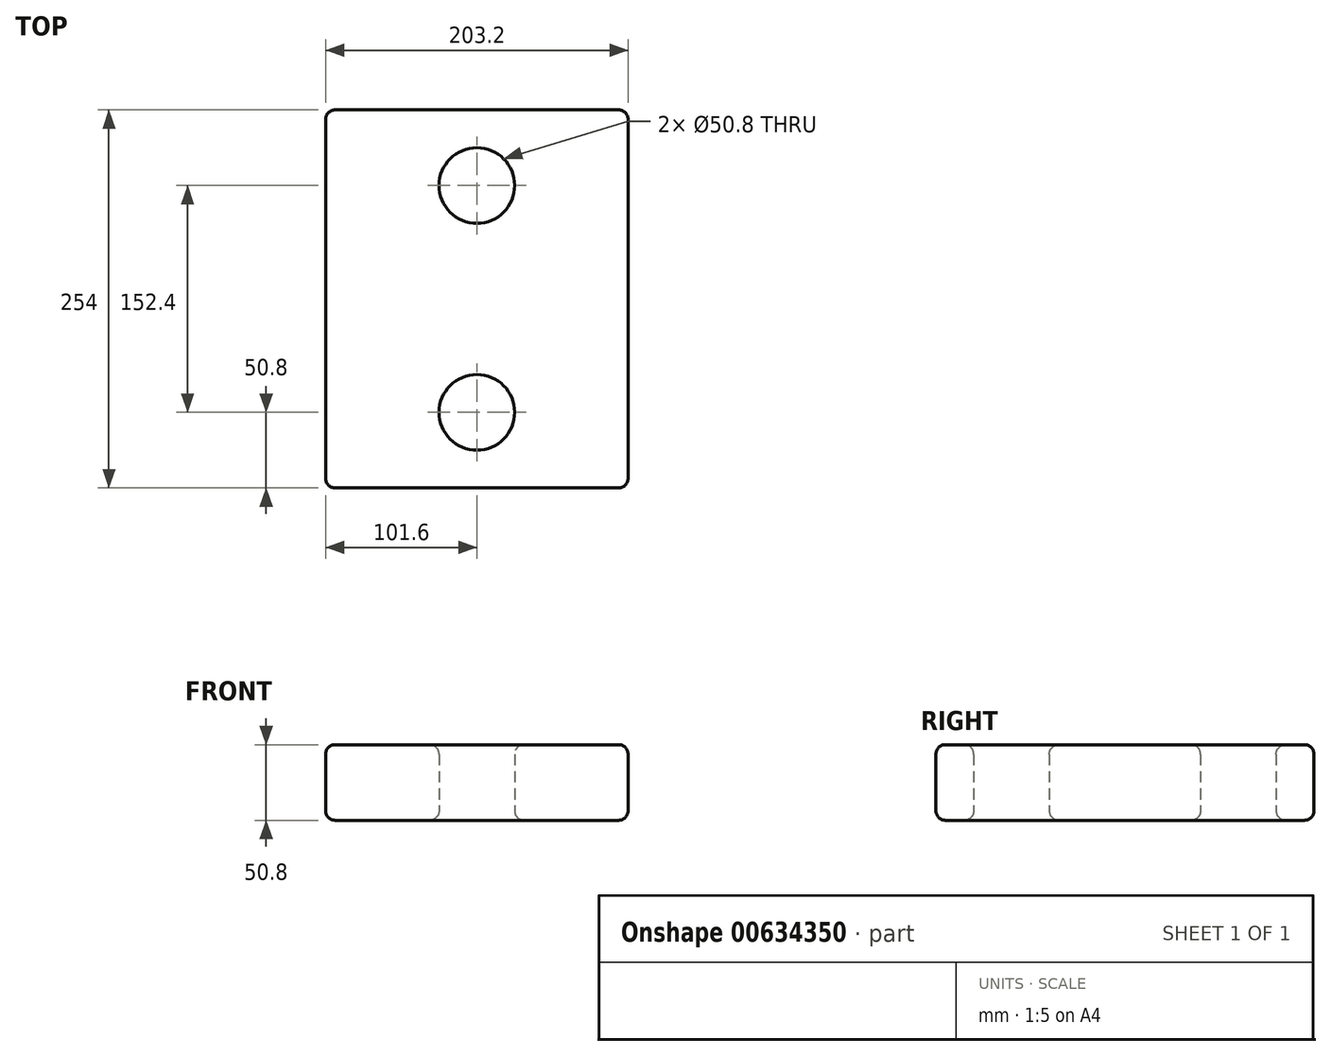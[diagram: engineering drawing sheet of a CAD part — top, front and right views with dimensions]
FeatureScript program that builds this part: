
annotation { "Feature Type Name" : "Feature", "Feature Type Description" : "" }
export const myFeature = defineFeature(function(context is Context, id is Id, definition is map)
    precondition{}
    {
        {
            var Q0;
            Q0=qCreatedBy(makeId("Top.planeOp"),FACE);
            var sketch = newSketch(context, id + "F0", { "sketchPlane" : qUnion([Q0])});
            skLineSegment(sketch, "E0.bottom", {"start": v(0, 0) * mm, "end": v(203.2, 0) * mm});
            skLineSegment(sketch, "E0.top", {"start": v(0, 254) * mm, "end": v(203.2, 254) * mm});
            skLineSegment(sketch, "E0.left", {"start": v(0, 0) * mm, "end": v(0, 254) * mm});
            skLineSegment(sketch, "E0.right", {"start": v(203.2, 0) * mm, "end": v(203.2, 254) * mm});
            skCircle(sketch, "E1", {"center": v(101.6, 203.2) * mm, "radius": 25.4 * mm});
            skPoint(sketch, "E1.centerSnap0", {"position": v(101.6, 0) * mm});
            skLineSegment(sketch, "E2", {"start": v(0, 127) * mm, "end": v(203.2, 127) * mm, "construction": true});
            skCircle(sketch, "E3.MirrorC", {"center": v(101.6, 50.8) * mm, "radius": 25.4 * mm});
            skSolve(sketch);
        }
        {
            var Q0;
            Q0=makeQuery(id+"F0.imprint","IMPRINT",FACE,{"disambiguationData":[TD([[makeQuery(id+"F0.imprint","IMPRINT",EDGE,{"derivedFrom":sQuery(id+"F0.wireOp",EDGE,"E0.bottom")}),1.0]])]});
            extrude(context, id + "F1", {"entities" : qUnion([Q0]), "depth" : 50.8 * mm, "offsetDistance" : 25.4 * mm});
        }
        {
            var Q0;
            Q0=makeQuery(id+"F1.opExtrude","SWEPT_FACE",FACE,{"disambiguationData":[OSD([sQuery(id+"F0.wireOp",EDGE,"E0.left")])]});
            var Q1;
            Q1=makeQuery(id+"F1.opExtrude","SWEPT_FACE",FACE,{"disambiguationData":[OSD([sQuery(id+"F0.wireOp",EDGE,"E0.top")])]});
            var Q2;
            Q2=makeQuery(id+"F1.opExtrude","CAP_EDGE",EDGE,{"disambiguationData":[OSD([sQuery(id+"F0.wireOp",EDGE,"E1")])],"isStart":false});
            var Q3;
            Q3=makeQuery(id+"F1.opExtrude","CAP_EDGE",EDGE,{"disambiguationData":[OSD([sQuery(id+"F0.wireOp",EDGE,"E3.MirrorC")])],"isStart":false});
            var Q4;
            Q4=makeQuery(id+"F1.opExtrude","SWEPT_FACE",FACE,{"disambiguationData":[OSD([sQuery(id+"F0.wireOp",EDGE,"E3.MirrorC")])]});
            var Q5;
            Q5=makeQuery(id+"F1.opExtrude","SWEPT_FACE",FACE,{"disambiguationData":[OSD([sQuery(id+"F0.wireOp",EDGE,"E1")])]});
            var Q6;
            Q6=makeQuery(id+"F1.opExtrude","SWEPT_FACE",FACE,{"disambiguationData":[OSD([sQuery(id+"F0.wireOp",EDGE,"E0.bottom")])]});
            var Q7;
            Q7=makeQuery(id+"F1.opExtrude","SWEPT_FACE",FACE,{"disambiguationData":[OSD([sQuery(id+"F0.wireOp",EDGE,"E0.right")])]});
            fillet(context, id + "F2", {"entities" : qUnion([Q0, Q1, Q2, Q3, Q4, Q5, Q6, Q7]), "radius" : 6.35 * mm, "tangentPropagation" : true, "allowEdgeOverflow" : false});
        }
    });
